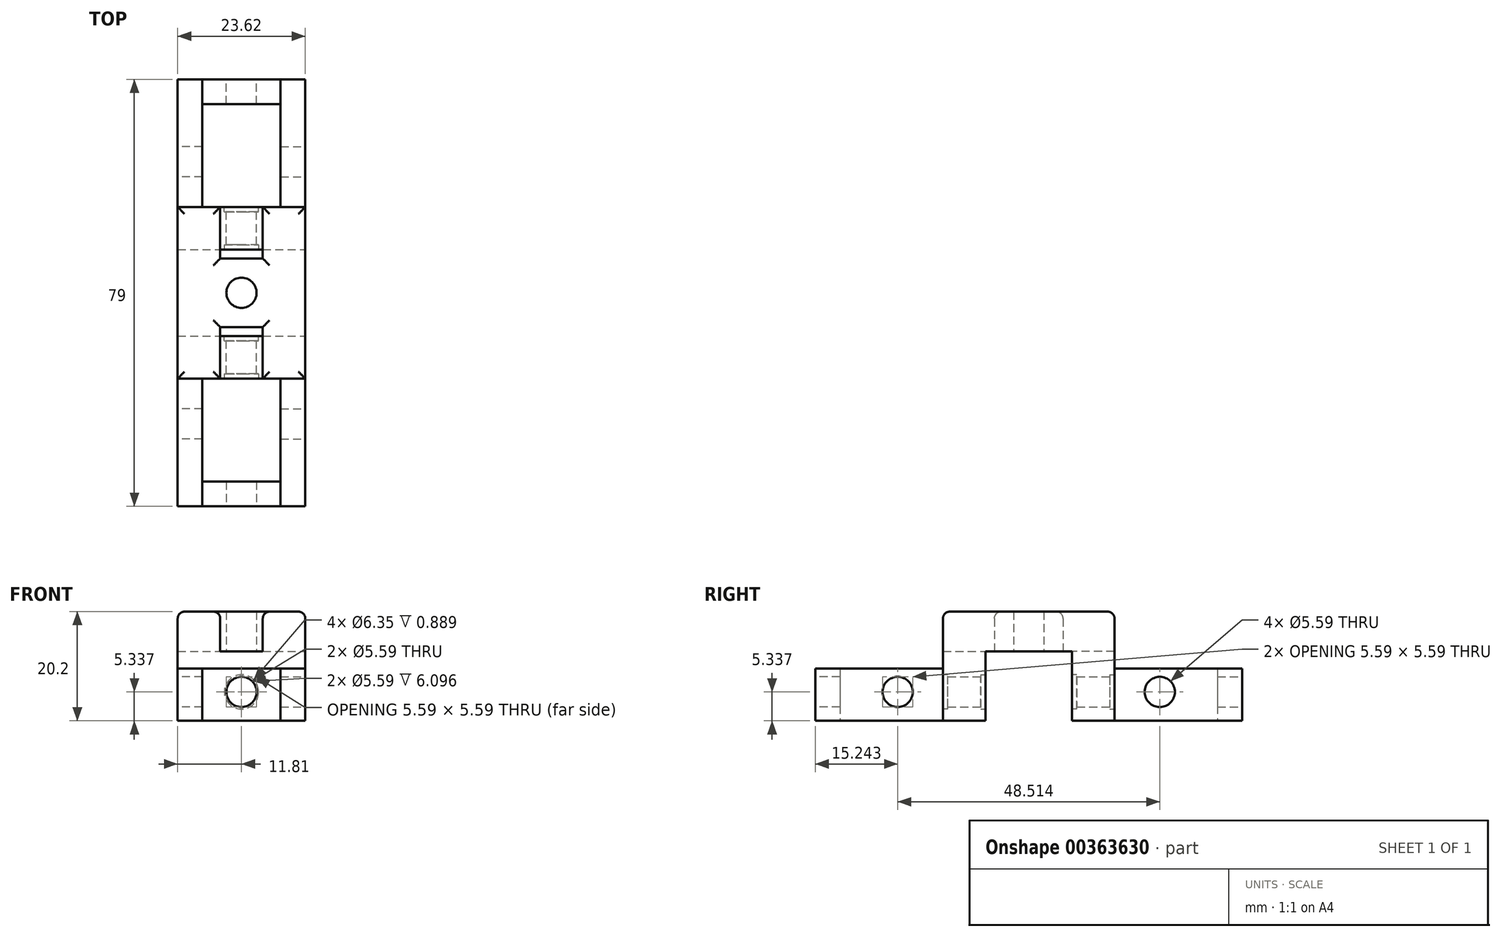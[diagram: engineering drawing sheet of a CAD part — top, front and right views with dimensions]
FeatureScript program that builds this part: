
annotation { "Feature Type Name" : "Feature", "Feature Type Description" : "" }
export const myFeature = defineFeature(function(context is Context, id is Id, definition is map)
    precondition{}
    {
        {
            var Q0;
            Q0=qCreatedBy(makeId("Top.planeOp"),FACE);
            var sketch = newSketch(context, id + "F0", { "sketchPlane" : qUnion([Q0])});
            skPoint(sketch, "E0.middle", {"position": v(0, 0) * mm});
            skCircle(sketch, "E1", {"center": v(0, 0) * mm, "radius": 2.8 * mm});
            skLineSegment(sketch, "E2", {"start": v(-11.81, 15.88) * mm, "end": v(-3.94, 15.88) * mm});
            skLineSegment(sketch, "E3", {"start": v(-3.94, 15.88) * mm, "end": v(-3.94, 6.35) * mm});
            skLineSegment(sketch, "E4", {"start": v(-3.94, 6.35) * mm, "end": v(0, 6.35) * mm});
            skLineSegment(sketch, "E5", {"start": v(-11.81, 15.88) * mm, "end": v(-11.81, 0) * mm});
            skLineSegment(sketch, "E6.MirrorCS", {"start": v(-11.81, -15.88) * mm, "end": v(-11.81, 0) * mm});
            skLineSegment(sketch, "E7.MirrorCS", {"start": v(-11.81, -15.88) * mm, "end": v(-3.94, -15.88) * mm});
            skLineSegment(sketch, "E8.MirrorCS", {"start": v(-3.94, -15.88) * mm, "end": v(-3.94, -6.35) * mm});
            skLineSegment(sketch, "E9.MirrorCS", {"start": v(-3.94, -6.35) * mm, "end": v(0, -6.35) * mm});
            skLineSegment(sketch, "E10.MirrorCS", {"start": v(3.94, 6.35) * mm, "end": v(0, 6.35) * mm});
            skLineSegment(sketch, "E11.MirrorCS", {"start": v(3.94, 15.88) * mm, "end": v(3.94, 6.35) * mm});
            skLineSegment(sketch, "E12.MirrorCS", {"start": v(11.81, 15.88) * mm, "end": v(3.94, 15.88) * mm});
            skLineSegment(sketch, "E13.MirrorCS", {"start": v(11.81, 15.88) * mm, "end": v(11.81, 0) * mm});
            skLineSegment(sketch, "E14.MirrorCS", {"start": v(11.81, -15.88) * mm, "end": v(11.81, 0) * mm});
            skLineSegment(sketch, "E15.MirrorCS", {"start": v(11.81, -15.88) * mm, "end": v(3.94, -15.88) * mm});
            skLineSegment(sketch, "E16.MirrorCS", {"start": v(3.94, -15.88) * mm, "end": v(3.94, -6.35) * mm});
            skLineSegment(sketch, "E17.MirrorCS", {"start": v(3.94, -6.35) * mm, "end": v(0, -6.35) * mm});
            skSolve(sketch);
        }
        {
            var Q0;
            Q0=makeQuery(id+"F0.imprint","IMPRINT",FACE,{"disambiguationData":[TD([[makeQuery(id+"F0.imprint","IMPRINT",EDGE,{"derivedFrom":sQuery(id+"F0.wireOp",EDGE,"E1")}),-1.0]])]});
            extrude(context, id + "F1", {"entities" : qUnion([Q0]), "depth" : 7.37 * mm});
        }
        {
            var Q0;
            Q0=makeQuery(id+"F1.opExtrude","CAP_FACE",FACE,{"disambiguationData":[OSD([sQuery(id+"F0.wireOp",EDGE,"E1"),sQuery(id+"F0.wireOp",EDGE,"E2"),sQuery(id+"F0.wireOp",EDGE,"E3"),sQuery(id+"F0.wireOp",EDGE,"E4"),sQuery(id+"F0.wireOp",EDGE,"E5"),sQuery(id+"F0.wireOp",EDGE,"E6.MirrorCS"),sQuery(id+"F0.wireOp",EDGE,"E7.MirrorCS"),sQuery(id+"F0.wireOp",EDGE,"E8.MirrorCS"),sQuery(id+"F0.wireOp",EDGE,"E9.MirrorCS"),sQuery(id+"F0.wireOp",EDGE,"E10.MirrorCS"),sQuery(id+"F0.wireOp",EDGE,"E11.MirrorCS"),sQuery(id+"F0.wireOp",EDGE,"E12.MirrorCS"),sQuery(id+"F0.wireOp",EDGE,"E13.MirrorCS"),sQuery(id+"F0.wireOp",EDGE,"E14.MirrorCS"),sQuery(id+"F0.wireOp",EDGE,"E15.MirrorCS"),sQuery(id+"F0.wireOp",EDGE,"E16.MirrorCS"),sQuery(id+"F0.wireOp",EDGE,"E17.MirrorCS")])],"isStart":true});
            var sketch = newSketch(context, id + "F2", { "sketchPlane" : qUnion([Q0])});
            skLineSegment(sketch, "E18", {"start": v(11.81, -15.88) * mm, "end": v(-11.81, -15.88) * mm});
            skLineSegment(sketch, "E19", {"start": v(-11.81, -15.88) * mm, "end": v(-11.81, -8) * mm});
            skLineSegment(sketch, "E20", {"start": v(-11.81, -8) * mm, "end": v(11.81, -8) * mm});
            skLineSegment(sketch, "E21", {"start": v(11.81, -8) * mm, "end": v(11.81, -15.88) * mm});
            skLineSegment(sketch, "E22.MirrorCS", {"start": v(-11.81, 8) * mm, "end": v(11.81, 8) * mm});
            skLineSegment(sketch, "E23.MirrorCS", {"start": v(11.81, 8) * mm, "end": v(11.81, 15.88) * mm});
            skLineSegment(sketch, "E24.MirrorCS", {"start": v(11.81, 15.88) * mm, "end": v(-11.81, 15.88) * mm});
            skLineSegment(sketch, "E25.MirrorCS", {"start": v(-11.81, 15.88) * mm, "end": v(-11.81, 8) * mm});
            skSolve(sketch);
        }
        {
            var Q0;
            Q0 = qSketchRegion(id + "F2", true);
            extrude(context, id + "F3", {"entities" : qUnion([Q0]), "operationType" : NewBodyOperationType.ADD, "depth" : 12.83 * mm});
        }
        {
            var Q0;
            Q0=makeQuery(id+"F3.boolean.opBoolean","MERGE",FACE,{"derivedFrom":[makeQuery(id+"F1.opExtrude","SWEPT_FACE",FACE,{"disambiguationData":[OSD([sQuery(id+"F0.wireOp",EDGE,"E2")])]}),makeQuery(id+"F1.opExtrude","SWEPT_FACE",FACE,{"disambiguationData":[OSD([sQuery(id+"F0.wireOp",EDGE,"E12.MirrorCS")])]}),makeQuery(id+"F3.opExtrude","SWEPT_FACE",FACE,{"disambiguationData":[OSD([sQuery(id+"F2.wireOp",EDGE,"E18")])]})]});
            var sketch = newSketch(context, id + "F4", { "sketchPlane" : qUnion([Q0])});
            skCircle(sketch, "E26", {"center": v(0, -7.5) * mm, "radius": 2.8 * mm});
            skSolve(sketch);
        }
        {
            var Q0;
            Q0=makeQuery(id+"F4.imprint","IMPRINT",FACE,{"disambiguationData":[TD([[makeQuery(id+"F4.imprint","IMPRINT",EDGE,{"derivedFrom":sQuery(id+"F4.wireOp",EDGE,"E26")}),1.0]])]});
            var Q1;
            Q1=makeQuery(id+"F3.boolean.opBoolean","MERGE",FACE,{"derivedFrom":[makeQuery(id+"F1.opExtrude","SWEPT_FACE",FACE,{"disambiguationData":[OSD([sQuery(id+"F0.wireOp",EDGE,"E7.MirrorCS")])]}),makeQuery(id+"F1.opExtrude","SWEPT_FACE",FACE,{"disambiguationData":[OSD([sQuery(id+"F0.wireOp",EDGE,"E15.MirrorCS")])]}),makeQuery(id+"F3.opExtrude","SWEPT_FACE",FACE,{"disambiguationData":[OSD([sQuery(id+"F2.wireOp",EDGE,"E24.MirrorCS")])]})]});
            extrude(context, id + "F5", {"entities" : qUnion([Q0]), "operationType" : NewBodyOperationType.REMOVE, "endBound" : BoundingType.UP_TO_SURFACE, "oppositeDirection" : true, "endBoundEntityFace" : qUnion([Q1]), "depth" : 25.4 * mm});
        }
        {
            var Q0;
            Q0=makeQuery(id+"F3.boolean.opBoolean","MERGE",FACE,{"derivedFrom":[makeQuery(id+"F1.opExtrude","SWEPT_FACE",FACE,{"disambiguationData":[OSD([sQuery(id+"F0.wireOp",EDGE,"E7.MirrorCS")])]}),makeQuery(id+"F1.opExtrude","SWEPT_FACE",FACE,{"disambiguationData":[OSD([sQuery(id+"F0.wireOp",EDGE,"E15.MirrorCS")])]}),makeQuery(id+"F3.opExtrude","SWEPT_FACE",FACE,{"disambiguationData":[OSD([sQuery(id+"F2.wireOp",EDGE,"E24.MirrorCS")])]})]});
            var sketch = newSketch(context, id + "F6", { "sketchPlane" : qUnion([Q0])});
            skLineSegment(sketch, "E27", {"start": v(-11.81, -12.83) * mm, "end": v(-11.81, -3.18) * mm});
            skLineSegment(sketch, "E28", {"start": v(-11.81, -3.18) * mm, "end": v(-7.24, -3.18) * mm});
            skLineSegment(sketch, "E29", {"start": v(-7.24, -3.18) * mm, "end": v(-7.24, -12.83) * mm});
            skLineSegment(sketch, "E30", {"start": v(-7.24, -12.83) * mm, "end": v(-11.81, -12.83) * mm});
            skSolve(sketch);
        }
        {
            var Q0;
            Q0=makeQuery(id+"F6.imprint","IMPRINT",FACE,{"disambiguationData":[TD([[makeQuery(id+"F6.imprint","IMPRINT",EDGE,{"derivedFrom":sQuery(id+"F6.wireOp",EDGE,"E27")}),1.0]])]});
            extrude(context, id + "F7", {"entities" : qUnion([Q0]), "depth" : 23.62 * mm});
        }
        {
            var Q0;
            Q0=makeQuery(id+"F7.opExtrude","SWEPT_FACE",FACE,{"disambiguationData":[OSD([sQuery(id+"F6.wireOp",EDGE,"E27")])]});
            var sketch = newSketch(context, id + "F8", { "sketchPlane" : qUnion([Q0])});
            skCircle(sketch, "E31", {"center": v(24.26, -7.5) * mm, "radius": 2.8 * mm});
            skSolve(sketch);
        }
        {
            var Q0;
            Q0=makeQuery(id+"F8.imprint","IMPRINT",FACE,{"disambiguationData":[TD([[makeQuery(id+"F8.imprint","IMPRINT",EDGE,{"derivedFrom":sQuery(id+"F8.wireOp",EDGE,"E31")}),1.0]])]});
            var Q1;
            Q1=makeQuery(id+"F7.opExtrude","SWEPT_FACE",FACE,{"disambiguationData":[OSD([sQuery(id+"F6.wireOp",EDGE,"E29")])]});
            extrude(context, id + "F9", {"entities" : qUnion([Q0]), "operationType" : NewBodyOperationType.REMOVE, "endBound" : BoundingType.UP_TO_SURFACE, "oppositeDirection" : true, "endBoundEntityFace" : qUnion([Q1]), "depth" : 25.4 * mm});
        }
        {
            var Q0;
            Q0=makeQuery(id+"F7.opExtrude","SWEPT_BODY",BODY,{"disambiguationData":[OSD([sQuery(id+"F6.wireOp",EDGE,"E27"),sQuery(id+"F6.wireOp",EDGE,"E28"),sQuery(id+"F6.wireOp",EDGE,"E29"),sQuery(id+"F6.wireOp",EDGE,"E30")])]});
            var Q1;
            Q1=qCreatedBy(makeId("Right.planeOp"),FACE);
            mirror(context, id + "F10", {"entities" : qUnion([Q0]), "mirrorPlane" : qUnion([Q1])});
        }
        {
            var Q0;
            Q0=makeQuery(id+"F10.opPattern","COPY",FACE,{"derivedFrom":makeQuery(id+"F7.opExtrude","SWEPT_FACE",FACE,{"disambiguationData":[OSD([sQuery(id+"F6.wireOp",EDGE,"E29")])]}),"instanceName":"1"});
            var sketch = newSketch(context, id + "F11", { "sketchPlane" : qUnion([Q0])});
            skLineSegment(sketch, "E32.bottom", {"start": v(39.5, -12.83) * mm, "end": v(34.93, -12.83) * mm});
            skLineSegment(sketch, "E32.top", {"start": v(39.5, -3.17) * mm, "end": v(34.93, -3.17) * mm});
            skLineSegment(sketch, "E32.left", {"start": v(39.5, -12.83) * mm, "end": v(39.5, -3.17) * mm});
            skLineSegment(sketch, "E32.right", {"start": v(34.93, -12.83) * mm, "end": v(34.93, -3.17) * mm});
            skSolve(sketch);
        }
        {
            var Q0;
            Q0=makeQuery(id+"F11.imprint","IMPRINT",FACE,{"disambiguationData":[TD([[makeQuery(id+"F11.imprint","IMPRINT",EDGE,{"derivedFrom":sQuery(id+"F11.wireOp",EDGE,"E32.bottom")}),-1.0]])]});
            var Q1;
            Q1=makeQuery(id+"F7.opExtrude","SWEPT_FACE",FACE,{"disambiguationData":[OSD([sQuery(id+"F6.wireOp",EDGE,"E29")])]});
            extrude(context, id + "F12", {"entities" : qUnion([Q0]), "endBound" : BoundingType.UP_TO_SURFACE, "endBoundEntityFace" : qUnion([Q1]), "depth" : 25.4 * mm});
        }
        {
            var Q0;
            Q0=makeQuery(id+"F12.opExtrude","SWEPT_FACE",FACE,{"disambiguationData":[OSD([sQuery(id+"F11.wireOp",EDGE,"E32.left")])]});
            var sketch = newSketch(context, id + "F13", { "sketchPlane" : qUnion([Q0])});
            skCircle(sketch, "E33", {"center": v(0, -7.5) * mm, "radius": 2.8 * mm});
            skSolve(sketch);
        }
        {
            var Q0;
            Q0=makeQuery(id+"F13.imprint","IMPRINT",FACE,{"disambiguationData":[TD([[makeQuery(id+"F13.imprint","IMPRINT",EDGE,{"derivedFrom":sQuery(id+"F13.wireOp",EDGE,"E33")}),1.0]])]});
            var Q1;
            Q1=makeQuery(id+"F12.opExtrude","SWEPT_FACE",FACE,{"disambiguationData":[OSD([sQuery(id+"F11.wireOp",EDGE,"E32.right")])]});
            extrude(context, id + "F14", {"entities" : qUnion([Q0]), "operationType" : NewBodyOperationType.REMOVE, "endBound" : BoundingType.UP_TO_SURFACE, "oppositeDirection" : true, "endBoundEntityFace" : qUnion([Q1]), "depth" : 25.4 * mm});
        }
        {
            var Q0;
            Q0=makeQuery(id+"F7.opExtrude","SWEPT_BODY",BODY,{"disambiguationData":[OSD([sQuery(id+"F6.wireOp",EDGE,"E27"),sQuery(id+"F6.wireOp",EDGE,"E28"),sQuery(id+"F6.wireOp",EDGE,"E29"),sQuery(id+"F6.wireOp",EDGE,"E30")])]});
            var Q1;
            Q1=makeQuery(id+"F12.opExtrude","SWEPT_BODY",BODY,{"disambiguationData":[OSD([sQuery(id+"F11.wireOp",EDGE,"E32.bottom"),sQuery(id+"F11.wireOp",EDGE,"E32.top"),sQuery(id+"F11.wireOp",EDGE,"E32.left"),sQuery(id+"F11.wireOp",EDGE,"E32.right")])]});
            var Q2;
            Q2=makeQuery(id+"F10.opPattern","COPY",BODY,{"derivedFrom":makeQuery(id+"F7.opExtrude","SWEPT_BODY",BODY,{"disambiguationData":[OSD([sQuery(id+"F6.wireOp",EDGE,"E27"),sQuery(id+"F6.wireOp",EDGE,"E28"),sQuery(id+"F6.wireOp",EDGE,"E29"),sQuery(id+"F6.wireOp",EDGE,"E30")])]}),"instanceName":"1"});
            var Q3;
            Q3=qCreatedBy(makeId("Front.planeOp"),FACE);
            mirror(context, id + "F15", {"entities" : qUnion([Q0, Q1, Q2]), "mirrorPlane" : qUnion([Q3])});
        }
        {
            var Q0;
            Q0=makeQuery(id+"F1.opExtrude","CAP_EDGE",EDGE,{"disambiguationData":[OSD([sQuery(id+"F0.wireOp",EDGE,"E5"),sQuery(id+"F0.wireOp",EDGE,"E6.MirrorCS")])],"isStart":false});
            var Q1;
            Q1=makeQuery(id+"F1.opExtrude","CAP_EDGE",EDGE,{"disambiguationData":[OSD([sQuery(id+"F0.wireOp",EDGE,"E2")])],"isStart":false});
            var Q2;
            Q2=makeQuery(id+"F1.opExtrude","CAP_EDGE",EDGE,{"disambiguationData":[OSD([sQuery(id+"F0.wireOp",EDGE,"E3")])],"isStart":false});
            var Q3;
            Q3=makeQuery(id+"F1.opExtrude","CAP_EDGE",EDGE,{"disambiguationData":[OSD([sQuery(id+"F0.wireOp",EDGE,"E4"),sQuery(id+"F0.wireOp",EDGE,"E10.MirrorCS")])],"isStart":false});
            var Q4;
            Q4=makeQuery(id+"F1.opExtrude","CAP_EDGE",EDGE,{"disambiguationData":[OSD([sQuery(id+"F0.wireOp",EDGE,"E11.MirrorCS")])],"isStart":false});
            var Q5;
            Q5=makeQuery(id+"F1.opExtrude","CAP_EDGE",EDGE,{"disambiguationData":[OSD([sQuery(id+"F0.wireOp",EDGE,"E12.MirrorCS")])],"isStart":false});
            var Q6;
            Q6=makeQuery(id+"F1.opExtrude","CAP_EDGE",EDGE,{"disambiguationData":[OSD([sQuery(id+"F0.wireOp",EDGE,"E13.MirrorCS"),sQuery(id+"F0.wireOp",EDGE,"E14.MirrorCS")])],"isStart":false});
            var Q7;
            Q7=makeQuery(id+"F1.opExtrude","CAP_EDGE",EDGE,{"disambiguationData":[OSD([sQuery(id+"F0.wireOp",EDGE,"E15.MirrorCS")])],"isStart":false});
            var Q8;
            Q8=makeQuery(id+"F1.opExtrude","CAP_EDGE",EDGE,{"disambiguationData":[OSD([sQuery(id+"F0.wireOp",EDGE,"E16.MirrorCS")])],"isStart":false});
            var Q9;
            Q9=makeQuery(id+"F1.opExtrude","CAP_EDGE",EDGE,{"disambiguationData":[OSD([sQuery(id+"F0.wireOp",EDGE,"E9.MirrorCS"),sQuery(id+"F0.wireOp",EDGE,"E17.MirrorCS")])],"isStart":false});
            var Q10;
            Q10=makeQuery(id+"F1.opExtrude","CAP_EDGE",EDGE,{"disambiguationData":[OSD([sQuery(id+"F0.wireOp",EDGE,"E7.MirrorCS")])],"isStart":false});
            var Q11;
            Q11=makeQuery(id+"F1.opExtrude","CAP_EDGE",EDGE,{"disambiguationData":[OSD([sQuery(id+"F0.wireOp",EDGE,"E8.MirrorCS")])],"isStart":false});
            fillet(context, id + "F16", {"entities" : qUnion([Q0, Q1, Q2, Q3, Q4, Q5, Q6, Q7, Q8, Q9, Q10, Q11]), "radius" : 1.27 * mm, "tangentPropagation" : true, "allowEdgeOverflow" : false});
        }
        {
            var Q0;
            Q0=makeQuery(id+"F3.opExtrude","SWEPT_FACE",FACE,{"disambiguationData":[OSD([sQuery(id+"F2.wireOp",EDGE,"E20")])]});
            var sketch = newSketch(context, id + "F17", { "sketchPlane" : qUnion([Q0])});
            skCircle(sketch, "E34", {"center": v(0, -7.5) * mm, "radius": 3.18 * mm});
            skSolve(sketch);
        }
        {
            var Q0;
            Q0 = qSketchRegion(id + "F17", true);
            extrude(context, id + "F18", {"entities" : qUnion([Q0]), "operationType" : NewBodyOperationType.REMOVE, "oppositeDirection" : true, "depth" : 0.89 * mm});
        }
        {
            var Q0;
            Q0=makeQuery(id+"F3.opExtrude","SWEPT_FACE",FACE,{"disambiguationData":[OSD([sQuery(id+"F2.wireOp",EDGE,"E22.MirrorCS")])]});
            var sketch = newSketch(context, id + "F19", { "sketchPlane" : qUnion([Q0])});
            skCircle(sketch, "E35", {"center": v(0, -7.5) * mm, "radius": 3.18 * mm});
            skSolve(sketch);
        }
        {
            var Q0;
            Q0=makeQuery(id+"F19.imprint","IMPRINT",FACE,{"disambiguationData":[TD([[makeQuery(id+"F19.imprint","IMPRINT",EDGE,{"derivedFrom":sQuery(id+"F19.wireOp",EDGE,"E35")}),1.0]])]});
            extrude(context, id + "F20", {"entities" : qUnion([Q0]), "operationType" : NewBodyOperationType.REMOVE, "oppositeDirection" : true, "offsetDistance" : 25.4 * mm, "depth" : 0.89 * mm});
        }
        {
            var Q0;
            Q0=makeQuery(id+"F3.boolean.opBoolean","MERGE",FACE,{"derivedFrom":[makeQuery(id+"F1.opExtrude","SWEPT_FACE",FACE,{"disambiguationData":[OSD([sQuery(id+"F0.wireOp",EDGE,"E7.MirrorCS")])]}),makeQuery(id+"F1.opExtrude","SWEPT_FACE",FACE,{"disambiguationData":[OSD([sQuery(id+"F0.wireOp",EDGE,"E15.MirrorCS")])]}),makeQuery(id+"F3.opExtrude","SWEPT_FACE",FACE,{"disambiguationData":[OSD([sQuery(id+"F2.wireOp",EDGE,"E24.MirrorCS")])]})]});
            var sketch = newSketch(context, id + "F21", { "sketchPlane" : qUnion([Q0])});
            skCircle(sketch, "E36", {"center": v(0, -7.5) * mm, "radius": 3.18 * mm});
            skSolve(sketch);
        }
        {
            var Q0;
            Q0=makeQuery(id+"F21.imprint","IMPRINT",FACE,{"disambiguationData":[TD([[makeQuery(id+"F21.imprint","IMPRINT",EDGE,{"derivedFrom":sQuery(id+"F21.wireOp",EDGE,"E36")}),1.0]])]});
            var Q1;
            Q1=sQuery(id+"F21.wireOp",EDGE,"E36");
            extrude(context, id + "F22", {"entities" : qUnion([Q0]), "operationType" : NewBodyOperationType.REMOVE, "surfaceEntities" : qUnion([Q1]), "oppositeDirection" : true, "depth" : 0.89 * mm});
        }
        {
            var Q0;
            Q0=makeQuery(id+"F3.boolean.opBoolean","MERGE",FACE,{"derivedFrom":[makeQuery(id+"F1.opExtrude","SWEPT_FACE",FACE,{"disambiguationData":[OSD([sQuery(id+"F0.wireOp",EDGE,"E2")])]}),makeQuery(id+"F1.opExtrude","SWEPT_FACE",FACE,{"disambiguationData":[OSD([sQuery(id+"F0.wireOp",EDGE,"E12.MirrorCS")])]}),makeQuery(id+"F3.opExtrude","SWEPT_FACE",FACE,{"disambiguationData":[OSD([sQuery(id+"F2.wireOp",EDGE,"E18")])]})]});
            var sketch = newSketch(context, id + "F23", { "sketchPlane" : qUnion([Q0])});
            skCircle(sketch, "E37", {"center": v(0, -7.5) * mm, "radius": 3.18 * mm});
            skSolve(sketch);
        }
        {
            var Q0;
            Q0=makeQuery(id+"F23.imprint","IMPRINT",FACE,{"disambiguationData":[TD([[makeQuery(id+"F23.imprint","IMPRINT",EDGE,{"derivedFrom":sQuery(id+"F23.wireOp",EDGE,"E37")}),1.0]])]});
            var Q1;
            Q1 = qConstructionFilter(qBodyType(qCreatedBy(id + "F23" ,EDGE), BodyType.WIRE), ConstructionObject.NO);
            extrude(context, id + "F24", {"entities" : qUnion([Q0]), "operationType" : NewBodyOperationType.REMOVE, "surfaceEntities" : qUnion([Q1]), "oppositeDirection" : true, "depth" : 0.89 * mm});
        }
    });
